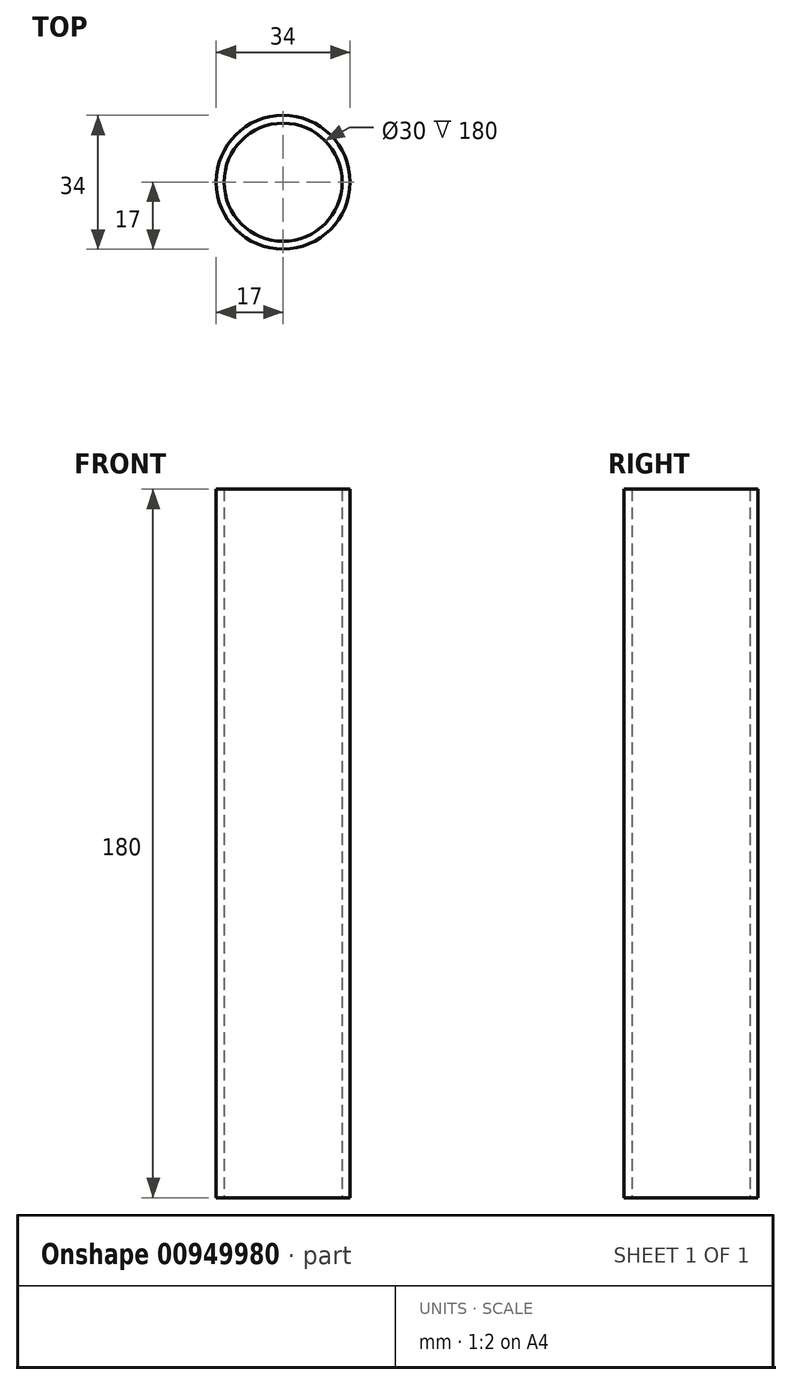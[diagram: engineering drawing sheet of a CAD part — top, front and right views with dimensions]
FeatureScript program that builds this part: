
annotation { "Feature Type Name" : "Feature", "Feature Type Description" : "" }
export const myFeature = defineFeature(function(context is Context, id is Id, definition is map)
    precondition{}
    {
        {
            var Q0;
            Q0=qCreatedBy(makeId("Top.planeOp"),FACE);
            var sketch = newSketch(context, id + "F0", { "sketchPlane" : qUnion([Q0])});
            skCircle(sketch, "E0", {"center": v(0, 0) * mm, "radius": 15 * mm});
            skCircle(sketch, "E1", {"center": v(0, 0) * mm, "radius": 17 * mm});
            skSolve(sketch);
        }
        {
            var Q0;
            Q0=makeQuery(id+"F0.imprint","IMPRINT",FACE,{"disambiguationData":[TD([[makeQuery(id+"F0.imprint","IMPRINT",EDGE,{"derivedFrom":sQuery(id+"F0.wireOp",EDGE,"E0")}),-1.0]])]});
            extrude(context, id + "F1", {"entities" : qUnion([Q0]), "depth" : 180 * mm, "offsetDistance" : 25 * mm});
        }
    });
